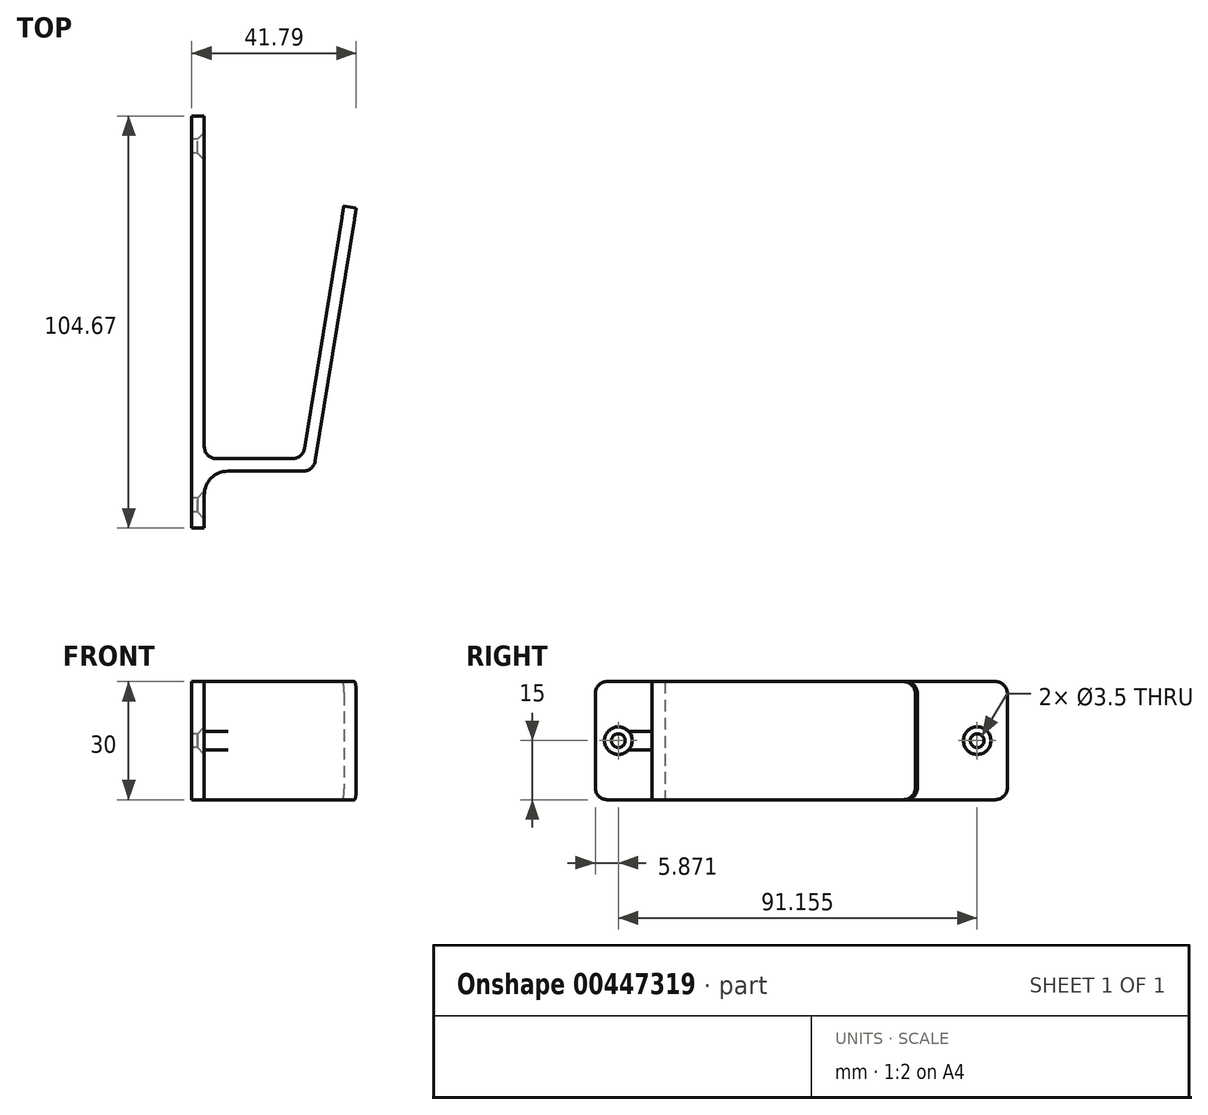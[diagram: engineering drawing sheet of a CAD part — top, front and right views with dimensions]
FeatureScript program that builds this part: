
annotation { "Feature Type Name" : "Feature", "Feature Type Description" : "" }
export const myFeature = defineFeature(function(context is Context, id is Id, definition is map)
    precondition{}
    {
        {
            var Q0;
            Q0=qCreatedBy(makeId("Top.planeOp"),FACE);
            var sketch = newSketch(context, id + "F0", { "sketchPlane" : qUnion([Q0])});
            skLineSegment(sketch, "E0", {"start": v(-18.21, 36.56) * mm, "end": v(-18.21, -53.44) * mm});
            skLineSegment(sketch, "E1", {"start": v(-18.21, 36.56) * mm, "end": v(-15.01, 36.56) * mm});
            skLineSegment(sketch, "E2", {"start": v(-15.01, 36.56) * mm, "end": v(-15.01, -50.44) * mm});
            skLineSegment(sketch, "E3", {"start": v(-15.01, -50.44) * mm, "end": v(9.99, -50.44) * mm});
            skLineSegment(sketch, "E4", {"start": v(9.99, -50.44) * mm, "end": v(20.42, 13.72) * mm});
            skLineSegment(sketch, "E5", {"start": v(20.42, 13.72) * mm, "end": v(23.58, 13.2) * mm});
            skLineSegment(sketch, "E6", {"start": v(23.58, 13.2) * mm, "end": v(12.7, -53.64) * mm});
            skLineSegment(sketch, "E7", {"start": v(12.7, -53.64) * mm, "end": v(-15.01, -53.64) * mm});
            skLineSegment(sketch, "E8", {"start": v(-18.21, -53.44) * mm, "end": v(-18.21, -68.1) * mm});
            skLineSegment(sketch, "E9", {"start": v(-18.21, -68.1) * mm, "end": v(-15.01, -68.1) * mm});
            skLineSegment(sketch, "E10", {"start": v(-15.01, -68.1) * mm, "end": v(-15.01, -53.64) * mm});
            skSolve(sketch);
        }
        {
            var Q0;
            Q0=makeQuery(id+"F0.imprint","IMPRINT",FACE,{"disambiguationData":[TD([[makeQuery(id+"F0.imprint","IMPRINT",EDGE,{"derivedFrom":sQuery(id+"F0.wireOp",EDGE,"E0")}),1.0]])]});
            extrude(context, id + "F1", {"entities" : qUnion([Q0]), "flatOperationType" : FlatOperationType.REMOVE, "offsetDistance" : 25 * mm, "depth" : 30 * mm, "domain" : OperationDomain.MODEL});
        }
        {
            var Q0;
            Q0=makeQuery(id+"F1.opExtrude","SWEPT_EDGE",EDGE,{"disambiguationData":[OSD([sQuery(id+"F0.wireOp",EDGE,"E6"),sQuery(id+"F0.wireOp",EDGE,"E7")])]});
            var Q1;
            Q1=makeQuery(id+"F1.opExtrude","SWEPT_EDGE",EDGE,{"disambiguationData":[OSD([sQuery(id+"F0.wireOp",EDGE,"E6"),sQuery(id+"F0.wireOp",EDGE,"E7")])]});
            var Q2;
            Q2=makeQuery(id+"F1.opExtrude","SWEPT_EDGE",EDGE,{"disambiguationData":[OSD([sQuery(id+"F0.wireOp",EDGE,"E2"),sQuery(id+"F0.wireOp",EDGE,"E3")])]});
            var Q3;
            Q3=makeQuery(id+"F1.opExtrude","SWEPT_EDGE",EDGE,{"disambiguationData":[OSD([sQuery(id+"F0.wireOp",EDGE,"E3"),sQuery(id+"F0.wireOp",EDGE,"E4")])]});
            var Q4;
            Q4=makeQuery(id+"F1.opExtrude","CAP_EDGE",EDGE,{"disambiguationData":[OSD([sQuery(id+"F0.wireOp",EDGE,"E5")])],"isStart":false});
            var Q5;
            Q5=makeQuery(id+"F1.opExtrude","CAP_EDGE",EDGE,{"disambiguationData":[OSD([sQuery(id+"F0.wireOp",EDGE,"E5")])],"isStart":true});
            var Q6;
            Q6=makeQuery(id+"F1.opExtrude","CAP_EDGE",EDGE,{"disambiguationData":[OSD([sQuery(id+"F0.wireOp",EDGE,"E1")])],"isStart":true});
            var Q7;
            Q7=makeQuery(id+"F1.opExtrude","CAP_EDGE",EDGE,{"disambiguationData":[OSD([sQuery(id+"F0.wireOp",EDGE,"E1")])],"isStart":false});
            var Q8;
            Q8=makeQuery(id+"F1.opExtrude","CAP_EDGE",EDGE,{"disambiguationData":[OSD([sQuery(id+"F0.wireOp",EDGE,"E9")])],"isStart":true});
            var Q9;
            Q9=makeQuery(id+"F1.opExtrude","CAP_EDGE",EDGE,{"disambiguationData":[OSD([sQuery(id+"F0.wireOp",EDGE,"E9")])],"isStart":false});
            fillet(context, id + "F2", {"entities" : qUnion([Q0, Q1, Q2, Q3, Q4, Q5, Q6, Q7, Q8, Q9]), "radius" : 3 * mm, "tangentPropagation" : true, "allowEdgeOverflow" : false});
        }
        {
            var Q0;
            Q0=makeQuery(id+"F1.opExtrude","SWEPT_FACE",FACE,{"disambiguationData":[OSD([sQuery(id+"F0.wireOp",EDGE,"E2")])]});
            var sketch = newSketch(context, id + "F3", { "sketchPlane" : qUnion([Q0])});
            skLineSegment(sketch, "E11", {"start": v(45.8, 15) * mm, "end": v(-79.19, 15) * mm, "construction": true});
            skPoint(sketch, "E11.startSnap0", {"position": v(36.56, 15) * mm});
            skPoint(sketch, "E11.endSnap0", {"position": v(36.56, 15) * mm});
            skCircle(sketch, "E12", {"center": v(28.92, 15) * mm, "radius": 1.75 * mm});
            skCircle(sketch, "E13", {"center": v(-62.24, 15) * mm, "radius": 1.75 * mm});
            skSolve(sketch);
        }
        {
            var Q0;
            Q0=sQuery(id+"F3.wireOp",VERTEX,"E12.center");
            var Q1;
            Q1=sQuery(id+"F3.wireOp",VERTEX,"E13.center");
            var Q2;
            Q2=makeQuery(id+"F1.opExtrude","SWEPT_BODY",BODY,{"disambiguationData":[OSD([sQuery(id+"F0.wireOp",EDGE,"E0"),sQuery(id+"F0.wireOp",EDGE,"E1"),sQuery(id+"F0.wireOp",EDGE,"E2"),sQuery(id+"F0.wireOp",EDGE,"E3"),sQuery(id+"F0.wireOp",EDGE,"E4"),sQuery(id+"F0.wireOp",EDGE,"E5"),sQuery(id+"F0.wireOp",EDGE,"E6"),sQuery(id+"F0.wireOp",EDGE,"E7")])]});
            hole(context, id + "F4", {"style" : HoleStyle.C_SINK, "endStyle" : HoleEndStyle.BLIND, "holeDiameter" : 3.5 * mm, "cSinkDiameter" : 7 * mm, "cSinkAngle" : 90 * degree, "holeDepth" : 30 * mm, "isTappedThrough" : true, "tappedDepth" : 12 * mm, "tapClearance" : 3, "startFromSketch" : true, "locations" : qUnion([Q0, Q1]), "scope" : qUnion([Q2])});
        }
        {
            var Q0;
            Q0=makeQuery(id+"F1.opExtrude","SWEPT_EDGE",EDGE,{"disambiguationData":[OSD([sQuery(id+"F0.wireOp",EDGE,"E7"),sQuery(id+"F0.wireOp",EDGE,"E10")])]});
            fillet(context, id + "F5", {"entities" : qUnion([Q0]), "radius" : 6 * mm, "tangentPropagation" : true, "allowEdgeOverflow" : false});
        }
    });
